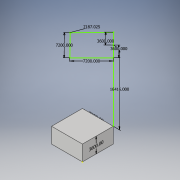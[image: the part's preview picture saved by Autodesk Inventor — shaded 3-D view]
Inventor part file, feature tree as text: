
AUTODESK INVENTOR PART (.ipt)
format: ipt  version: 2018 (Build 220112000, 112)  size: 114,176 bytes
history: native  units: in
note: dims shown in document units (in); Inventor stores cm internally (conversion verified against a paired STEP export)
features: sketch x6, other x3, extrude x1
ambient origin geometry x8: Origin, YZ Plane, XZ Plane, XY Plane, X Axis, Y Axis, Z Axis, Center Point
bodies: Solid1 (feature_tree)
feature tree (10):
  other  "Annotations"
  sketch  "Sketch1"  dims[d0=7200.0in d1=7200.0in]
  extrude  "Extrusion1"  Depth=7200.0in
  sketch  "3D Sketch9"
  sketch  "3D Sketch12"
  sketch  "3D Sketch13"
  sketch  "3D Sketch14"
  sketch  "Sketch2"  dims[d2=3600.0in d3=0.0in d17=16416.0in d20=3600.0in d21=3600.0in d26=7200.0in d27=7200.0in d28=7187.0251in d22=0.1318in d23=3600.0in d24=7200.0in]
  other  "Linear Dimension 1"
  other  "Linear Dimension 2"
